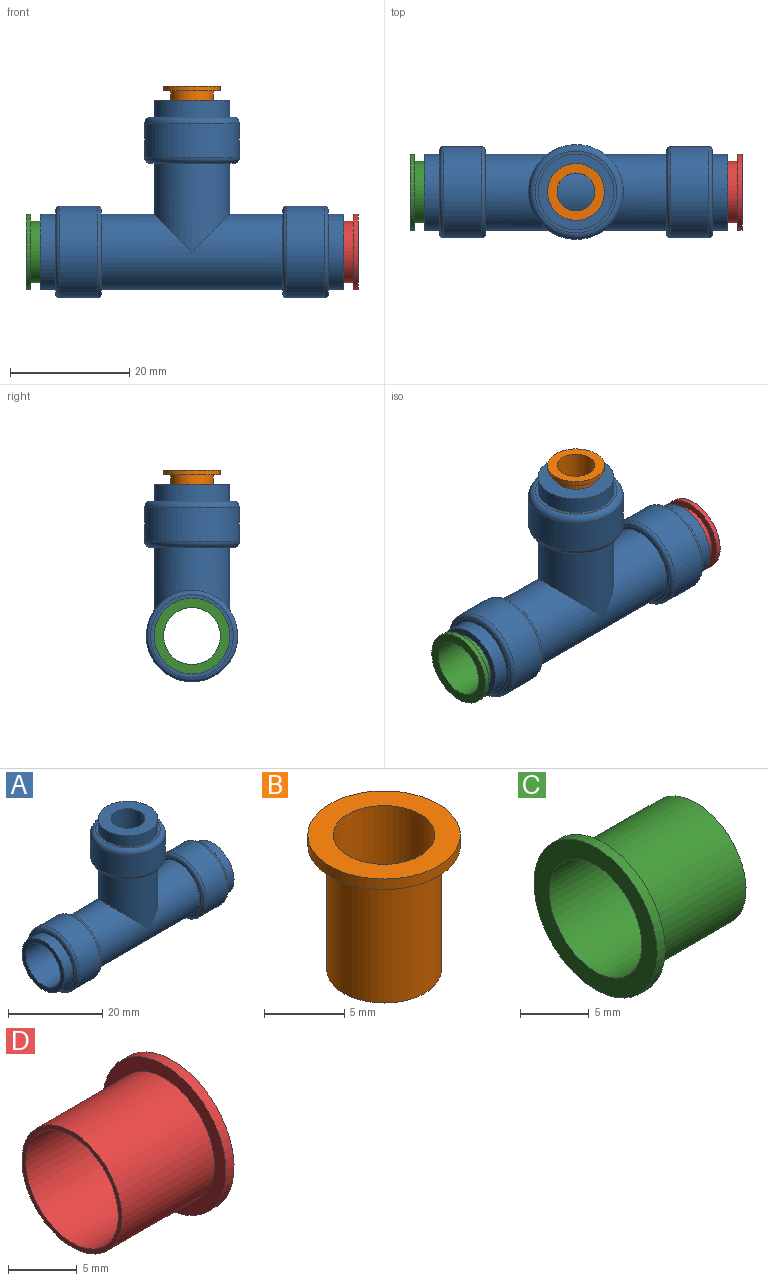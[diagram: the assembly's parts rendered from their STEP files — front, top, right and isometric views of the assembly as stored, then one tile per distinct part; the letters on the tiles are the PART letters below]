
ASSEMBLY  parts=4 mates=3
PART A: 26 faces, bbox 50.8x17.2x33.7 mm
  f0: cylinder r=6.35mm len=14.84mm, axis (0,0,-1), area 430.7mm2, adj f1,f17
  f1: cylinder r=6.35mm len=30.34mm, axis (-1,0,0), area 1049.2mm2, adj f0,f3,f10
  f2: torus R=6.93mm, axis (1,0,0), area 53.3mm2, adj f3,f6
  f3: plane 13.87x13.87mm, normal (-1,0,0), area 24.4mm2, adj f1,f2
  f4: plane 13.87x13.87mm, normal (1,0,0), area 24.4mm2, adj f5,f7
  f5: torus R=6.93mm, axis (1,0,0), area 53.3mm2, adj f4,f6
  f6: cylinder r=7.66mm len=15.33mm, axis (1,0,0), area 300.4mm2, adj f2,f5
  f7: cylinder r=6.35mm len=12.7mm, axis (-1,0,0), area 101mm2, adj f4,f8
  f8: plane 12.7x12.7mm, normal (1,0,0), area 43.1mm2, adj f7,f25
  f9: torus R=6.93mm, axis (-1,0,0), area 53.3mm2, adj f10,f13
  f10: plane 13.87x13.87mm, normal (1,0,0), area 24.4mm2, adj f1,f9
  f11: plane 13.87x13.87mm, normal (-1,0,0), area 24.4mm2, adj f12,f14
  f12: torus R=6.93mm, axis (-1,0,0), area 53.3mm2, adj f11,f13
  f13: cylinder r=7.66mm len=15.33mm, axis (-1,0,0), area 300.4mm2, adj f9,f12
  f14: cylinder r=6.35mm len=12.7mm, axis (-1,0,0), area 101mm2, adj f11,f15
  f15: plane 12.7x12.7mm, normal (-1,0,0), area 43.1mm2, adj f14,f25
  f16: plane 13.69x13.69mm, normal (0,0,1), area 20.4mm2, adj f20,f24
  f17: plane 13.86x13.86mm, normal (0,0,-1), area 24.2mm2, adj f0,f18
  f18: torus R=6.93mm, axis (0,0,1), area 75.7mm2, adj f17,f19
  f19: cylinder r=7.94mm len=15.88mm, axis (0,0,1), area 282.8mm2, adj f18,f20
  f20: torus R=6.84mm, axis (0,0,1), area 81.8mm2, adj f16,f19
  f21: cylinder r=6.35mm len=7.15mm, axis (-1,0,0), area 41.9mm2, adj f22
  f22: cylinder r=3.57mm len=20.15mm, axis (0,0,-1), area 439.6mm2, adj f21,f23
  f23: plane 12.7x12.7mm, normal (0,0,1), area 86.6mm2, adj f22,f24
  f24: cylinder r=6.35mm len=12.7mm, axis (0,0,-1), area 111.1mm2, adj f16,f23
  f25: cylinder r=5.16mm len=50.8mm, axis (-1,0,0), area 1646.8mm2, adj f8,f15
PART B: 6 faces, bbox 9.5x9.5x10.3 mm
  f0: cylinder r=3.17mm len=10.32mm, axis (0,0,1), area 205.8mm2, adj f2,f4
  f1: cylinder r=3.57mm len=9.53mm, axis (0,0,1), area 213.8mm2, adj f2,f5
  f2: plane 7.14x7.14mm, normal (0,0,-1), area 8.4mm2, adj f0,f1
  f3: cylinder r=4.76mm len=9.53mm, axis (0,0,-1), area 23.8mm2, adj f4,f5
  f4: plane 9.53x9.53mm, normal (0,0,1), area 39.6mm2, adj f0,f3
  f5: plane 9.53x9.53mm, normal (0,0,-1), area 31.2mm2, adj f1,f3
PART C: 6 faces, bbox 10.4x12.7x12.7 mm
  f0: cylinder r=4.76mm len=10.35mm, axis (-1,0,0), area 309.7mm2, adj f2,f4
  f1: cylinder r=5.16mm len=10.32mm, axis (-1,0,0), area 308.8mm2, adj f2,f5
  f2: plane 10.32x10.32mm, normal (1,0,0), area 12.4mm2, adj f0,f1
  f3: cylinder r=6.35mm len=12.7mm, axis (1,0,0), area 32.9mm2, adj f4,f5
  f4: plane 12.7x12.7mm, normal (-1,0,0), area 55.4mm2, adj f0,f3
  f5: plane 12.7x12.7mm, normal (1,0,0), area 43.1mm2, adj f1,f3
PART D: 6 faces, bbox 10.4x12.7x12.7 mm
  f0: cylinder r=4.76mm len=10.35mm, axis (1,0,0), area 309.7mm2, adj f2,f4
  f1: cylinder r=5.16mm len=10.32mm, axis (1,0,0), area 308.8mm2, adj f2,f5
  f2: plane 10.32x10.32mm, normal (-1,0,0), area 12.4mm2, adj f0,f1
  f3: cylinder r=6.35mm len=12.7mm, axis (-1,0,0), area 32.9mm2, adj f4,f5
  f4: plane 12.7x12.7mm, normal (1,0,0), area 55.4mm2, adj f0,f3
  f5: plane 12.7x12.7mm, normal (-1,0,0), area 43.1mm2, adj f1,f3
PLACE A t=(-0.72,16.48,-3.85)mm
PLACE B t=(-0.72,16.48,-2.27)mm
PLACE C t=(-2.31,16.48,-3.85)mm
PLACE D t=(0.87,16.48,-3.85)mm
MATE fastened A.f22 <-> B.f0  axis (0,0,1) through (-0.72,16.48,21.55)mm
MATE fastened A.f25 <-> C.f0  axis (-1,0,0) through (-26.12,16.48,-3.85)mm
MATE fastened A.f25 <-> D.f0  axis (-1,0,0) through (24.68,16.48,-3.85)mm
